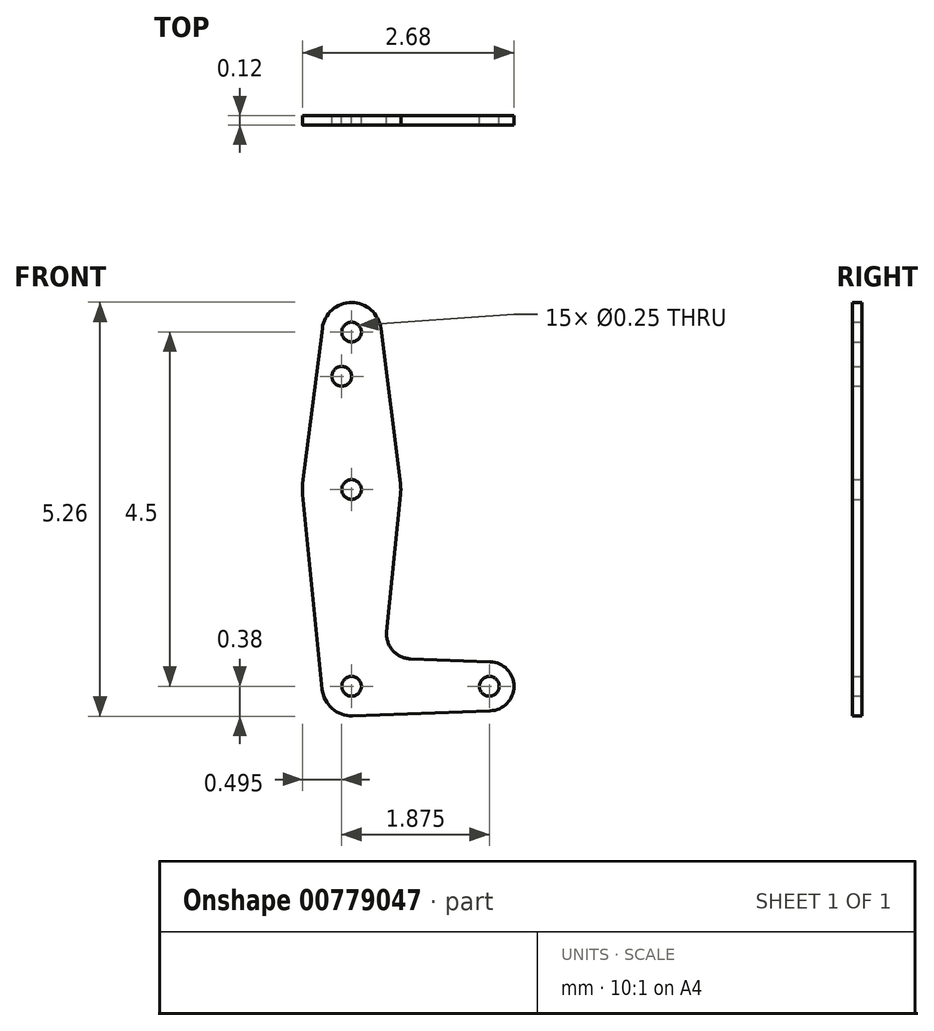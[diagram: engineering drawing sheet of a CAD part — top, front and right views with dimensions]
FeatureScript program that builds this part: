
annotation { "Feature Type Name" : "Feature", "Feature Type Description" : "" }
export const myFeature = defineFeature(function(context is Context, id is Id, definition is map)
    precondition{}
    {
        {
            var Q0;
            Q0=qCreatedBy(makeId("Front.planeOp"),FACE);
            var sketch = newSketch(context, id + "F0", { "sketchPlane" : qUnion([Q0])});
            skLineSegment(sketch, "E0", {"start": v(0, 4.5) * mm, "end": v(0, 0) * mm, "construction": true});
            skLineSegment(sketch, "E1", {"start": v(0, 0) * mm, "end": v(1.75, 0) * mm, "construction": true});
            skCircle(sketch, "E2", {"center": v(0, 4.5) * mm, "radius": 0.38 * mm});
            skCircle(sketch, "E3", {"center": v(0, 2.5) * mm, "radius": 0.62 * mm});
            skCircle(sketch, "E4", {"center": v(0, 0) * mm, "radius": 0.38 * mm});
            skCircle(sketch, "E5", {"center": v(1.75, 0) * mm, "radius": 0.31 * mm});
            skLineSegment(sketch, "E6", {"start": v(-0.37, 4.55) * mm, "end": v(-0.62, 2.58) * mm});
            skLineSegment(sketch, "E7", {"start": v(0.37, 4.55) * mm, "end": v(0.62, 2.58) * mm});
            skLineSegment(sketch, "E8", {"start": v(-0.62, 2.44) * mm, "end": v(-0.37, -0.04) * mm});
            skLineSegment(sketch, "E9", {"start": v(0.62, 2.44) * mm, "end": v(0.45, 0.7) * mm});
            skLineSegment(sketch, "E10", {"start": v(0.01, -0.37) * mm, "end": v(1.76, -0.31) * mm});
            skLineSegment(sketch, "E11", {"start": v(0.75, 0.35) * mm, "end": v(1.76, 0.31) * mm});
            skCircle(sketch, "E12", {"center": v(0, 4.5) * mm, "radius": 0.12 * mm});
            skCircle(sketch, "E13", {"center": v(-0.12, 3.94) * mm, "radius": 0.12 * mm});
            skCircle(sketch, "E14", {"center": v(0, 2.5) * mm, "radius": 0.12 * mm});
            skCircle(sketch, "E15", {"center": v(0, 0) * mm, "radius": 0.12 * mm});
            skCircle(sketch, "E16", {"center": v(1.75, 0) * mm, "radius": 0.12 * mm});
            skArc(sketch, "E17.filletArc", {"start": v(0.45, 0.7) * mm, "mid": v(0.52, 0.46) * mm, "end": v(0.75, 0.35) * mm});
            skSolve(sketch);
        }
        {
            var Q0;
            Q0 = qSketchRegion(id + "F0", true);
            extrude(context, id + "F1", {"entities" : qUnion([Q0]), "depth" : 0.12 * mm, "offsetDistance" : 25 * mm});
        }
    });
